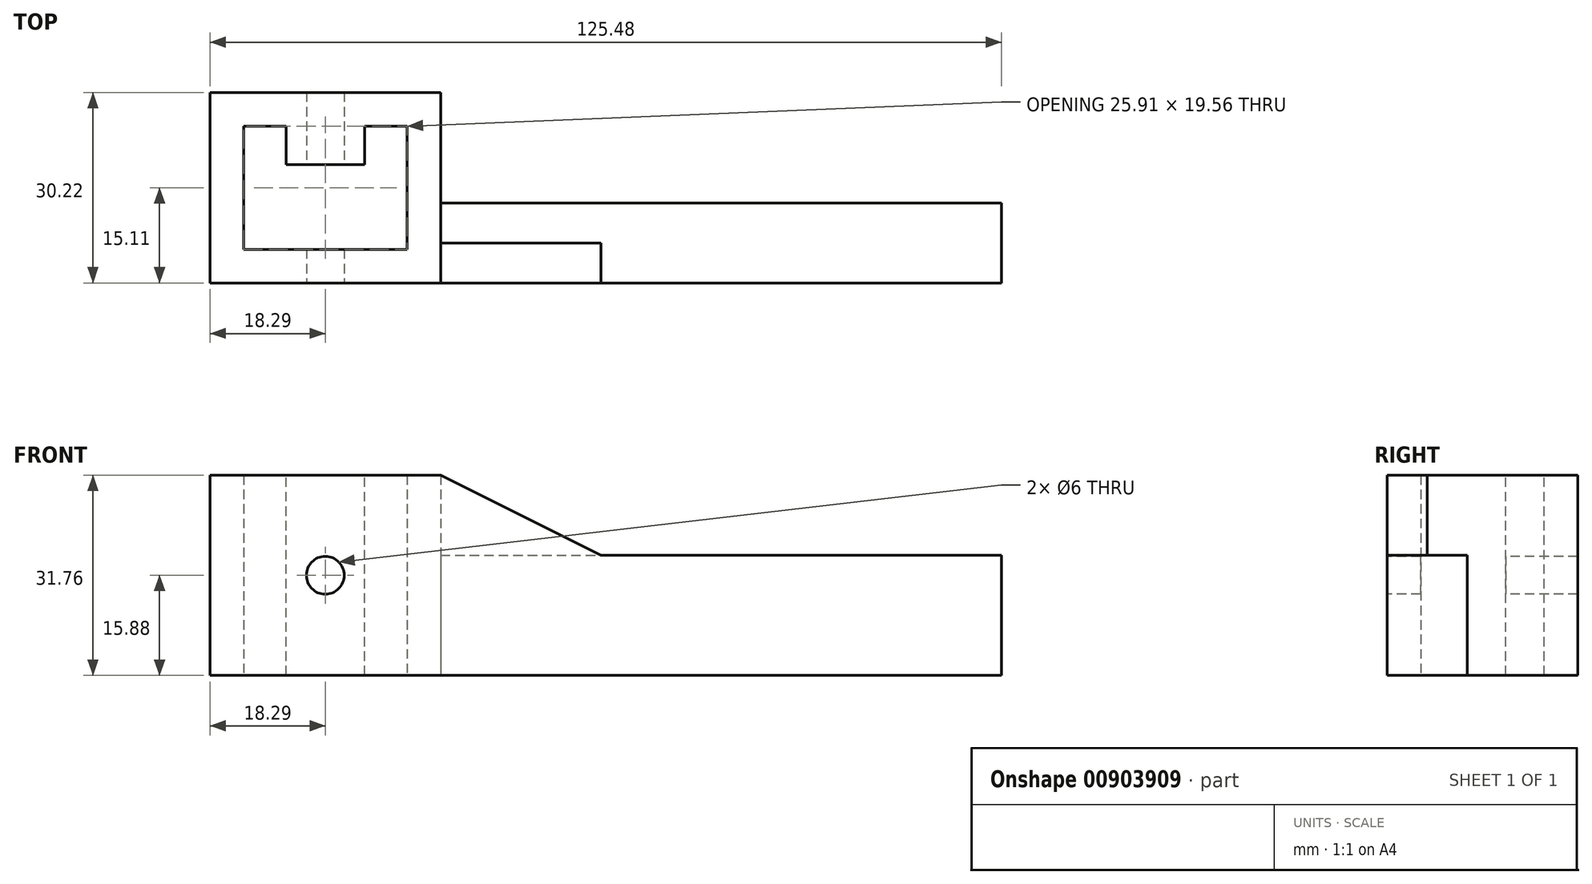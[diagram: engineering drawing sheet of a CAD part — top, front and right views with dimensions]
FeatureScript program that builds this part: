
annotation { "Feature Type Name" : "Feature", "Feature Type Description" : "" }
export const myFeature = defineFeature(function(context is Context, id is Id, definition is map)
    precondition{}
    {
        {
            var Q0;
            Q0=qCreatedBy(makeId("Top.planeOp"),FACE);
            var sketch = newSketch(context, id + "F0", { "sketchPlane" : qUnion([Q0])});
            skLineSegment(sketch, "E0.bottom", {"start": v(12.95, -9.78) * mm, "end": v(-12.95, -9.78) * mm});
            skLineSegment(sketch, "E0.top", {"start": v(12.95, 9.78) * mm, "end": v(-12.95, 9.78) * mm});
            skLineSegment(sketch, "E0.left", {"start": v(12.95, -9.78) * mm, "end": v(12.95, 9.78) * mm});
            skLineSegment(sketch, "E0.right", {"start": v(-12.95, -9.78) * mm, "end": v(-12.95, 9.78) * mm});
            skPoint(sketch, "E0.middle", {"position": v(0, 0) * mm});
            skLineSegment(sketch, "E1.0", {"start": v(-18.29, -15.11) * mm, "end": v(-18.29, 15.11) * mm});
            skLineSegment(sketch, "E1.1", {"start": v(18.29, -15.11) * mm, "end": v(-18.29, -15.11) * mm});
            skLineSegment(sketch, "E1.2", {"start": v(18.29, -15.11) * mm, "end": v(18.29, 15.11) * mm});
            skLineSegment(sketch, "E1.3", {"start": v(18.29, 15.11) * mm, "end": v(-18.29, 15.11) * mm});
            skSolve(sketch);
        }
        {
            var Q0;
            Q0=makeQuery(id+"F0.imprint","IMPRINT",FACE,{"disambiguationData":[TD([[makeQuery(id+"F0.imprint","IMPRINT",EDGE,{"derivedFrom":sQuery(id+"F0.wireOp",EDGE,"E0.bottom")}),1.0]])]});
            extrude(context, id + "F1", {"entities" : qUnion([Q0]), "endBound" : BoundingType.SYMMETRIC, "depth" : 31.75 * mm, "offsetDistance" : 25.4 * mm});
        }
        {
            var Q0;
            Q0=makeQuery(id+"F1.opExtrude","CAP_FACE",FACE,{"disambiguationData":[OSD([sQuery(id+"F0.wireOp",EDGE,"E0.bottom"),sQuery(id+"F0.wireOp",EDGE,"E0.top"),sQuery(id+"F0.wireOp",EDGE,"E0.left"),sQuery(id+"F0.wireOp",EDGE,"E0.right"),sQuery(id+"F0.wireOp",EDGE,"E1.0"),sQuery(id+"F0.wireOp",EDGE,"E1.1"),sQuery(id+"F0.wireOp",EDGE,"E1.2"),sQuery(id+"F0.wireOp",EDGE,"E1.3")])],"isStart":false});
            var sketch = newSketch(context, id + "F2", { "sketchPlane" : qUnion([Q0])});
            skLineSegment(sketch, "E2.bottom", {"start": v(6.22, 9.78) * mm, "end": v(-6.22, 9.78) * mm});
            skLineSegment(sketch, "E2.top", {"start": v(6.22, 3.68) * mm, "end": v(-6.22, 3.68) * mm});
            skLineSegment(sketch, "E2.left", {"start": v(6.22, 9.78) * mm, "end": v(6.22, 3.68) * mm});
            skLineSegment(sketch, "E2.right", {"start": v(-6.22, 9.78) * mm, "end": v(-6.22, 3.68) * mm});
            skPoint(sketch, "E2.middle", {"position": v(0, 6.73) * mm});
            skPoint(sketch, "E2.middle.positionSnap0", {"position": v(0, 9.78) * mm});
            skPoint(sketch, "E2.centerSnap0", {"position": v(0, 9.78) * mm});
            skSolve(sketch);
        }
        {
            var Q0;
            Q0=makeQuery(id+"F2.imprint","IMPRINT",FACE,{"disambiguationData":[TD([[makeQuery(id+"F2.imprint","IMPRINT",EDGE,{"derivedFrom":sQuery(id+"F2.wireOp",EDGE,"E2.bottom")}),1.0]])]});
            extrude(context, id + "F3", {"entities" : qUnion([Q0]), "operationType" : NewBodyOperationType.ADD, "oppositeDirection" : true, "depth" : 31.75 * mm, "offsetDistance" : 25.4 * mm});
        }
        {
            var Q0;
            Q0=makeQuery(id+"F3.boolean.opBoolean","MERGE",FACE,{"derivedFrom":[makeQuery(id+"F1.opExtrude","CAP_FACE",FACE,{"disambiguationData":[OSD([sQuery(id+"F0.wireOp",EDGE,"E0.bottom"),sQuery(id+"F0.wireOp",EDGE,"E0.top"),sQuery(id+"F0.wireOp",EDGE,"E0.left"),sQuery(id+"F0.wireOp",EDGE,"E0.right"),sQuery(id+"F0.wireOp",EDGE,"E1.0"),sQuery(id+"F0.wireOp",EDGE,"E1.1"),sQuery(id+"F0.wireOp",EDGE,"E1.2"),sQuery(id+"F0.wireOp",EDGE,"E1.3")])],"isStart":true}),makeQuery(id+"F3.opExtrude","CAP_FACE",FACE,{"disambiguationData":[OSD([sQuery(id+"F2.wireOp",EDGE,"E2.bottom"),sQuery(id+"F2.wireOp",EDGE,"E2.top"),sQuery(id+"F2.wireOp",EDGE,"E2.left"),sQuery(id+"F2.wireOp",EDGE,"E2.right")])],"isStart":false})]});
            var sketch = newSketch(context, id + "F4", { "sketchPlane" : qUnion([Q0])});
            skLineSegment(sketch, "E3.bottom", {"start": v(18.29, 15.11) * mm, "end": v(107.19, 15.11) * mm});
            skLineSegment(sketch, "E3.top", {"start": v(18.29, 2.41) * mm, "end": v(107.19, 2.41) * mm});
            skLineSegment(sketch, "E3.left", {"start": v(18.29, 15.11) * mm, "end": v(18.29, 2.41) * mm});
            skLineSegment(sketch, "E3.right", {"start": v(107.19, 15.11) * mm, "end": v(107.19, 2.41) * mm});
            skSolve(sketch);
        }
        {
            var Q0;
            Q0=makeQuery(id+"F4.imprint","IMPRINT",FACE,{"disambiguationData":[TD([[makeQuery(id+"F4.imprint","IMPRINT",EDGE,{"derivedFrom":sQuery(id+"F4.wireOp",EDGE,"E3.bottom")}),-1.0]])]});
            extrude(context, id + "F5", {"entities" : qUnion([Q0]), "operationType" : NewBodyOperationType.ADD, "oppositeDirection" : true, "depth" : 19.05 * mm, "offsetDistance" : 25.4 * mm});
        }
        {
            var Q0;
            Q0=makeQuery(id+"F5.boolean.opBoolean","MERGE",FACE,{"derivedFrom":[makeQuery(id+"F1.opExtrude","SWEPT_FACE",FACE,{"disambiguationData":[OSD([sQuery(id+"F0.wireOp",EDGE,"E1.1")])]}),makeQuery(id+"F5.opExtrude","SWEPT_FACE",FACE,{"disambiguationData":[OSD([sQuery(id+"F4.wireOp",EDGE,"E3.bottom")])]})]});
            var sketch = newSketch(context, id + "F6", { "sketchPlane" : qUnion([Q0])});
            skLineSegment(sketch, "E4", {"start": v(18.29, 15.88) * mm, "end": v(18.29, 3.18) * mm});
            skLineSegment(sketch, "E5", {"start": v(18.29, 3.18) * mm, "end": v(43.69, 3.18) * mm});
            skLineSegment(sketch, "E6", {"start": v(18.29, 15.88) * mm, "end": v(43.69, 3.18) * mm});
            skSolve(sketch);
        }
        {
            var Q0;
            Q0=qSketchRegion(id+"F6",true);
            extrude(context, id + "F7", {"entities" : qUnion([Q0]), "operationType" : NewBodyOperationType.ADD, "oppositeDirection" : true, "depth" : 6.35 * mm, "offsetDistance" : 25.4 * mm});
        }
        {
            var Q0;
            Q0=makeQuery(id+"F7.boolean.opBoolean","MERGE",FACE,{"derivedFrom":[makeQuery(id+"F5.boolean.opBoolean","MERGE",FACE,{"derivedFrom":[makeQuery(id+"F1.opExtrude","SWEPT_FACE",FACE,{"disambiguationData":[OSD([sQuery(id+"F0.wireOp",EDGE,"E1.1")])]}),makeQuery(id+"F5.opExtrude","SWEPT_FACE",FACE,{"disambiguationData":[OSD([sQuery(id+"F4.wireOp",EDGE,"E3.bottom")])]})]}),makeQuery(id+"F7.opExtrude","CAP_FACE",FACE,{"disambiguationData":[OSD([sQuery(id+"F6.wireOp",EDGE,"E4"),sQuery(id+"F6.wireOp",EDGE,"E5"),sQuery(id+"F6.wireOp",EDGE,"E6")])],"isStart":true})]});
            var sketch = newSketch(context, id + "F8", { "sketchPlane" : qUnion([Q0])});
            skSolve(sketch);
        }
        {
            var Q0;
            {var subQ1=sQuery(id+"F0.wireOp",EDGE,"E1.1");Q0=makeQuery(id+"F8.imprint","IMPRINT",FACE,{"disambiguationData":[TD([[makeQuery(id+"F8.imprint","IMPRINT",EDGE,{"derivedFrom":makeQuery(id+"F1.opExtrude","CAP_EDGE",EDGE,{"disambiguationData":[OSD([subQ1])],"isStart":false})}),1.0]])]});}
            var sketch = newSketch(context, id + "F9", { "sketchPlane" : qUnion([Q0])});
            skCircle(sketch, "E7", {"center": v(0, 0) * mm, "radius": 3 * mm});
            skSolve(sketch);
        }
        {
            var Q0;
            Q0=qSketchRegion(id+"F9",true);
            extrude(context, id + "F10", {"entities" : qUnion([Q0]), "operationType" : NewBodyOperationType.REMOVE, "endBound" : BoundingType.THROUGH_ALL, "oppositeDirection" : true, "depth" : 25.4 * mm, "offsetDistance" : 25.4 * mm});
        }
    });
